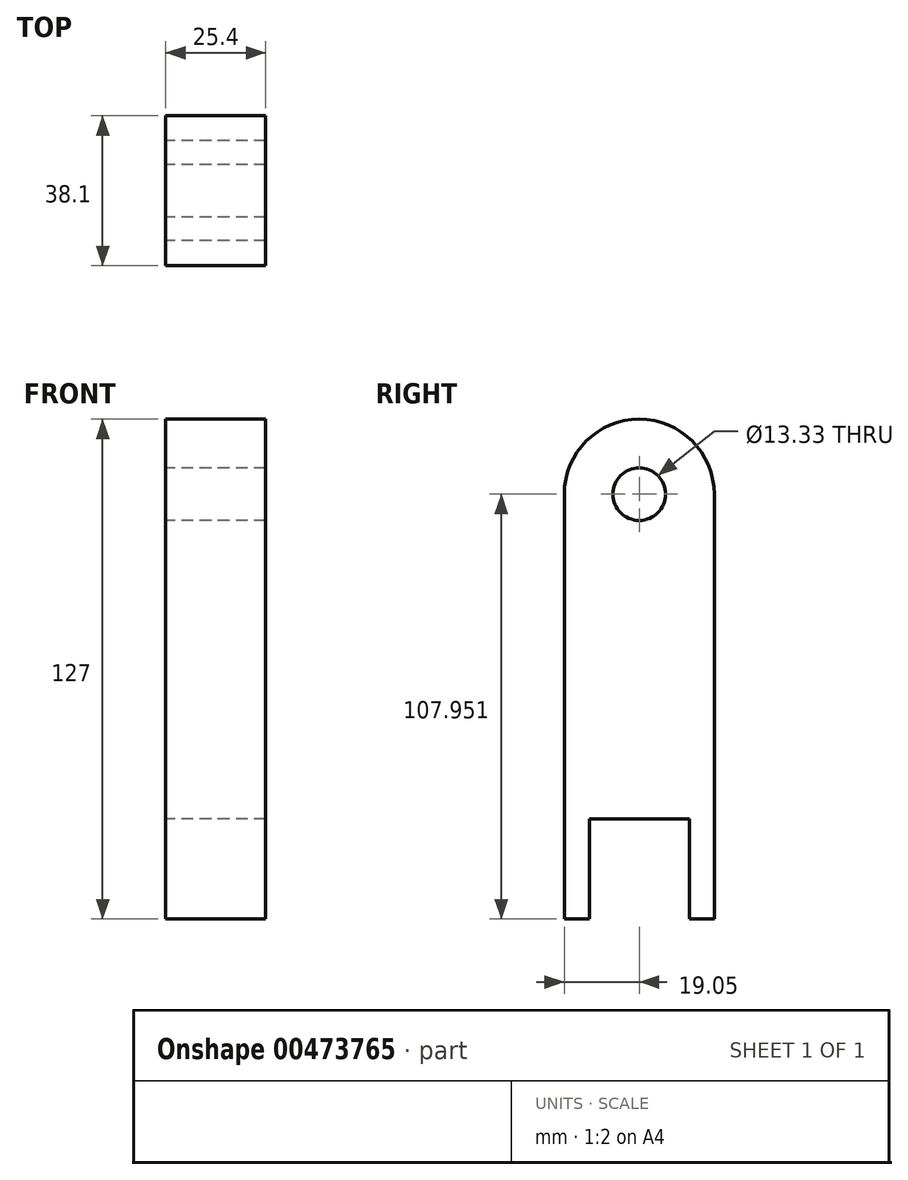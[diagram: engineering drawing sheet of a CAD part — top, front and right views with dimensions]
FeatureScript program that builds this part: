
annotation { "Feature Type Name" : "Feature", "Feature Type Description" : "" }
export const myFeature = defineFeature(function(context is Context, id is Id, definition is map)
    precondition{}
    {
        {
            var Q0;
            Q0=qCreatedBy(makeId("Right.planeOp"),FACE);
            var sketch = newSketch(context, id + "F0", { "sketchPlane" : qUnion([Q0])});
            skCircle(sketch, "E0", {"center": v(0, 66.22) * mm, "radius": 19.05 * mm});
            skLineSegment(sketch, "E1.bottom", {"start": v(19.05, 66.22) * mm, "end": v(-19.05, 66.22) * mm});
            skLineSegment(sketch, "E1.top", {"start": v(19.05, -16.33) * mm, "end": v(-19.05, -16.33) * mm});
            skLineSegment(sketch, "E1.left", {"start": v(19.05, 66.22) * mm, "end": v(19.05, -16.33) * mm});
            skLineSegment(sketch, "E1.right", {"start": v(-19.05, 66.22) * mm, "end": v(-19.05, -16.33) * mm});
            skLineSegment(sketch, "E2.bottom", {"start": v(-19.05, -16.33) * mm, "end": v(-12.7, -16.33) * mm});
            skLineSegment(sketch, "E2.top", {"start": v(-19.05, -41.73) * mm, "end": v(-12.7, -41.73) * mm});
            skLineSegment(sketch, "E2.left", {"start": v(-19.05, -16.33) * mm, "end": v(-19.05, -41.73) * mm});
            skLineSegment(sketch, "E2.right", {"start": v(-12.7, -16.33) * mm, "end": v(-12.7, -41.73) * mm});
            skLineSegment(sketch, "E3.bottom", {"start": v(19.05, -16.33) * mm, "end": v(12.7, -16.33) * mm});
            skLineSegment(sketch, "E3.top", {"start": v(19.05, -41.73) * mm, "end": v(12.7, -41.73) * mm});
            skLineSegment(sketch, "E3.left", {"start": v(19.05, -16.33) * mm, "end": v(19.05, -41.73) * mm});
            skLineSegment(sketch, "E3.right", {"start": v(12.7, -16.33) * mm, "end": v(12.7, -41.73) * mm});
            skCircle(sketch, "E4", {"center": v(0, 66.22) * mm, "radius": 6.67 * mm});
            skSolve(sketch);
        }
        {
            var Q0;
            Q0 = qSketchRegion(id + "F0", true);
            extrude(context, id + "F1", {"entities" : qUnion([Q0]), "depth" : 25.4 * mm});
        }
    });
